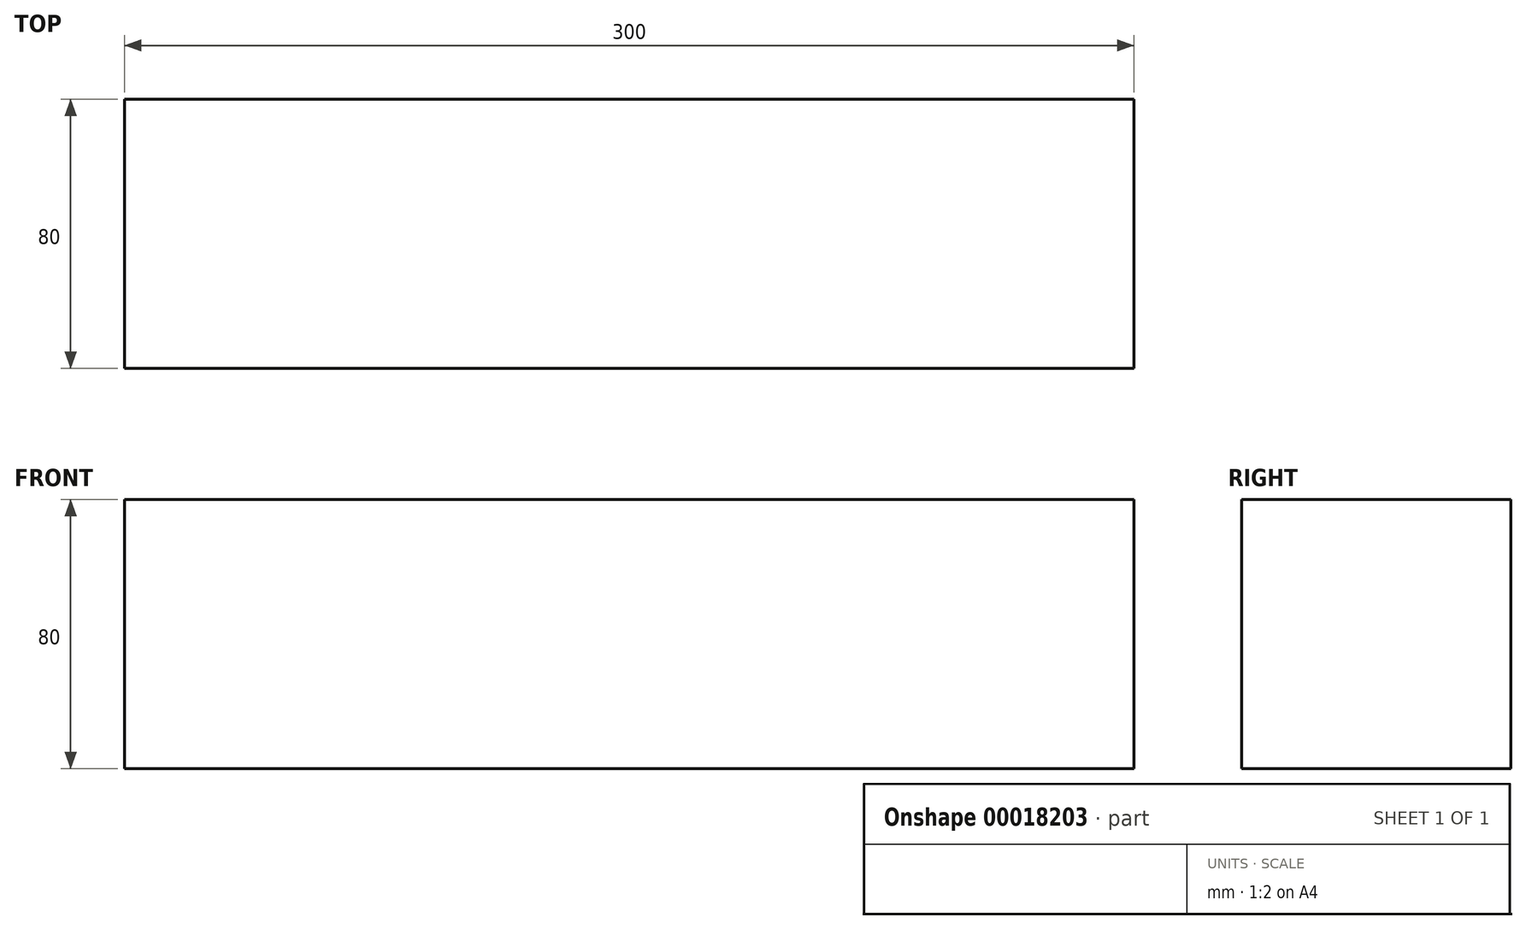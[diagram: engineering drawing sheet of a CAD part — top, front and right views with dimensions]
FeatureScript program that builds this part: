
annotation { "Feature Type Name" : "Feature", "Feature Type Description" : "" }
export const myFeature = defineFeature(function(context is Context, id is Id, definition is map)
    precondition{}
    {
        {
            var Q0;
            Q0=qCreatedBy(makeId("Top.planeOp"),FACE);
            var sketch = newSketch(context, id + "F0", { "sketchPlane" : qUnion([Q0])});
            skLineSegment(sketch, "E0.bottom", {"start": v(0, 0) * mm, "end": v(300, 0) * mm});
            skLineSegment(sketch, "E0.top", {"start": v(0, 80) * mm, "end": v(300, 80) * mm});
            skLineSegment(sketch, "E0.left", {"start": v(0, 0) * mm, "end": v(0, 80) * mm});
            skLineSegment(sketch, "E0.right", {"start": v(300, 0) * mm, "end": v(300, 80) * mm});
            skSolve(sketch);
        }
        {
            var Q0;
            Q0 = qSketchRegion(id + "F0", true);
            extrude(context, id + "F1", {"entities" : qUnion([Q0]), "depth" : 80 * mm});
        }
    });
